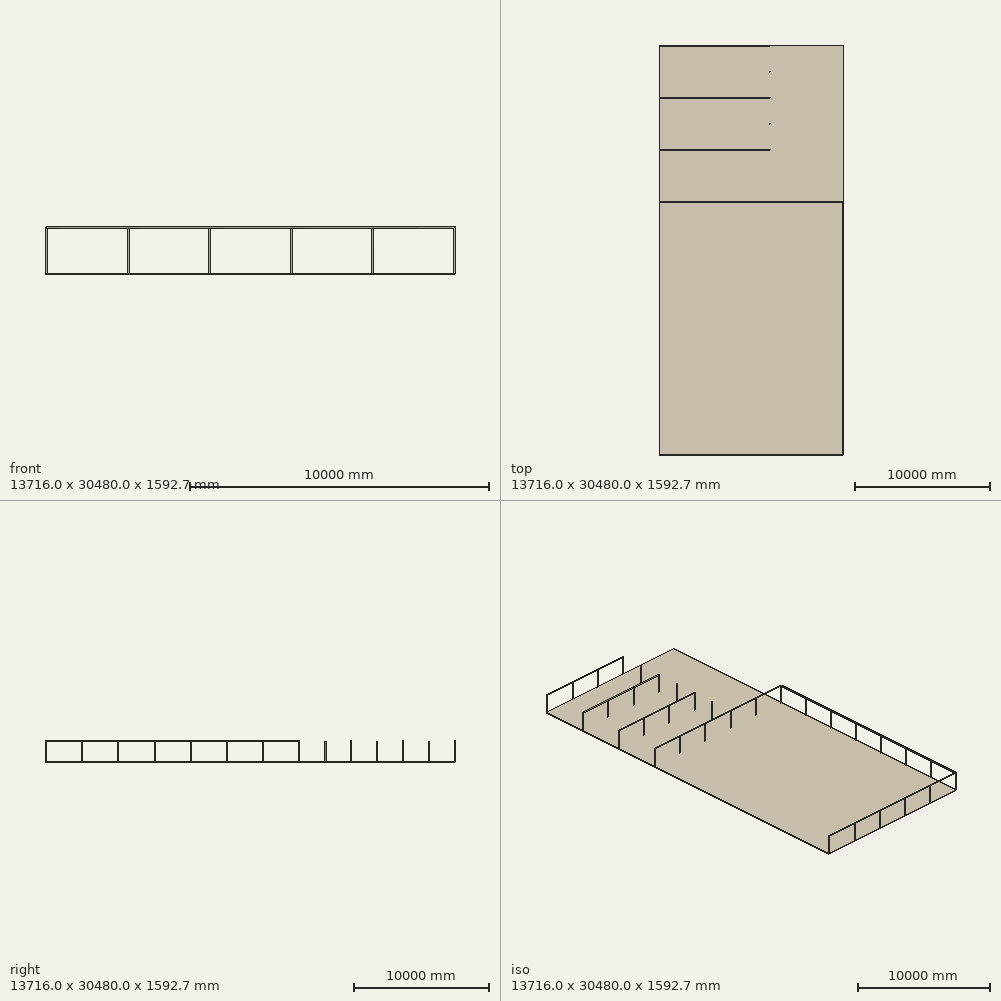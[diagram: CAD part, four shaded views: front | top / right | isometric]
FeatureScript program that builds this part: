
annotation { "Feature Type Name" : "Feature", "Feature Type Description" : "" }
export const myFeature = defineFeature(function(context is Context, id is Id, definition is map)
    precondition{}
    {
        {
            var Q0;
            Q0=qCreatedBy(makeId("Top.planeOp"),FACE);
            var sketch = newSketch(context, id + "F0", { "sketchPlane" : qUnion([Q0])});
            skLineSegment(sketch, "E0.bottom", {"start": v(0, 0) * mm, "end": v(13716, 0) * mm});
            skLineSegment(sketch, "E0.top", {"start": v(0, 30480) * mm, "end": v(13716, 30480) * mm});
            skLineSegment(sketch, "E0.left", {"start": v(0, 0) * mm, "end": v(0, 30480) * mm});
            skLineSegment(sketch, "E0.right", {"start": v(13716, 0) * mm, "end": v(13716, 30480) * mm});
            skSolve(sketch);
        }
        {
            var Q0;
            Q0 = qSketchRegion(id + "F0", true);
            extrude(context, id + "F1", {"entities" : qUnion([Q0]), "oppositeDirection" : true, "depth" : 30.48 * mm, "offsetDistance" : 30.48 * mm});
        }
        {
            var Q0;
            Q0=makeQuery(id+"F1.opExtrude","CAP_FACE",FACE,{"disambiguationData":[OSD([sQuery(id+"F0.wireOp",EDGE,"E0.bottom"),sQuery(id+"F0.wireOp",EDGE,"E0.top"),sQuery(id+"F0.wireOp",EDGE,"E0.left"),sQuery(id+"F0.wireOp",EDGE,"E0.right")])],"isStart":true});
            var sketch = newSketch(context, id + "F2", { "sketchPlane" : qUnion([Q0])});
            skLineSegment(sketch, "E1", {"start": v(38.1, 38.1) * mm, "end": v(2765.45, 38.1) * mm, "construction": true});
            skLineSegment(sketch, "E2", {"start": v(2765.45, 38.1) * mm, "end": v(5492.8, 38.1) * mm, "construction": true});
            skLineSegment(sketch, "E3", {"start": v(5492.8, 38.1) * mm, "end": v(8220.15, 38.1) * mm, "construction": true});
            skLineSegment(sketch, "E4", {"start": v(8220.15, 38.1) * mm, "end": v(10947.5, 38.1) * mm, "construction": true});
            skLineSegment(sketch, "E5", {"start": v(10947.5, 38.1) * mm, "end": v(13674.85, 38.1) * mm, "construction": true});
            skLineSegment(sketch, "E6", {"start": v(13674.85, 38.1) * mm, "end": v(13674.85, 2726.87) * mm, "construction": true});
            skLineSegment(sketch, "E7", {"start": v(13674.85, 2726.87) * mm, "end": v(13674.85, 5415.64) * mm, "construction": true});
            skLineSegment(sketch, "E8", {"start": v(13674.85, 5415.64) * mm, "end": v(13674.85, 8104.41) * mm, "construction": true});
            skLineSegment(sketch, "E9", {"start": v(13674.85, 8104.41) * mm, "end": v(13674.85, 10793.19) * mm, "construction": true});
            skLineSegment(sketch, "E10", {"start": v(13674.85, 10793.19) * mm, "end": v(13674.85, 13481.96) * mm, "construction": true});
            skLineSegment(sketch, "E11", {"start": v(13674.85, 13481.96) * mm, "end": v(13674.85, 16170.73) * mm, "construction": true});
            skLineSegment(sketch, "E12", {"start": v(13674.85, 16170.73) * mm, "end": v(13674.85, 18859.5) * mm, "construction": true});
            skLineSegment(sketch, "E13", {"start": v(13674.85, 18859.5) * mm, "end": v(10947.5, 18859.5) * mm, "construction": true});
            skLineSegment(sketch, "E14", {"start": v(10947.5, 18859.5) * mm, "end": v(8220.15, 18859.5) * mm, "construction": true});
            skLineSegment(sketch, "E15", {"start": v(8220.15, 18859.5) * mm, "end": v(5492.8, 18859.5) * mm, "construction": true});
            skLineSegment(sketch, "E16", {"start": v(5492.8, 18859.5) * mm, "end": v(2765.45, 18859.5) * mm, "construction": true});
            skLineSegment(sketch, "E17", {"start": v(2765.45, 18859.5) * mm, "end": v(38.1, 18859.5) * mm, "construction": true});
            skLineSegment(sketch, "E18", {"start": v(38.1, 18859.5) * mm, "end": v(38.1, 22720.3) * mm, "construction": true});
            skLineSegment(sketch, "E19", {"start": v(38.1, 22720.3) * mm, "end": v(38.1, 26581.1) * mm, "construction": true});
            skLineSegment(sketch, "E20", {"start": v(38.1, 26581.1) * mm, "end": v(38.1, 30441.9) * mm, "construction": true});
            skLineSegment(sketch, "E21", {"start": v(38.1, 30441.9) * mm, "end": v(2765.45, 30441.9) * mm, "construction": true});
            skLineSegment(sketch, "E22", {"start": v(2765.45, 30441.9) * mm, "end": v(5492.8, 30441.9) * mm, "construction": true});
            skLineSegment(sketch, "E23", {"start": v(5492.8, 30441.9) * mm, "end": v(8220.15, 30441.9) * mm, "construction": true});
            skLineSegment(sketch, "E24", {"start": v(38.1, 26581.1) * mm, "end": v(2765.45, 26581.1) * mm, "construction": true});
            skLineSegment(sketch, "E25", {"start": v(2765.45, 26581.1) * mm, "end": v(5492.8, 26581.1) * mm, "construction": true});
            skLineSegment(sketch, "E26", {"start": v(5492.8, 26581.1) * mm, "end": v(8220.15, 26581.1) * mm, "construction": true});
            skLineSegment(sketch, "E27", {"start": v(8220.15, 26581.1) * mm, "end": v(8220.15, 28536.9) * mm, "construction": true});
            skLineSegment(sketch, "E28", {"start": v(38.1, 22720.3) * mm, "end": v(2765.45, 22720.3) * mm, "construction": true});
            skLineSegment(sketch, "E29", {"start": v(2765.45, 22720.3) * mm, "end": v(5492.8, 22720.3) * mm, "construction": true});
            skLineSegment(sketch, "E30", {"start": v(5492.8, 22720.3) * mm, "end": v(8220.15, 22720.3) * mm, "construction": true});
            skLineSegment(sketch, "E31", {"start": v(8220.15, 22720.3) * mm, "end": v(8220.15, 24676.1) * mm, "construction": true});
            skLineSegment(sketch, "E32", {"start": v(8220.15, 18859.5) * mm, "end": v(8220.15, 20815.3) * mm, "construction": true});
            skCircle(sketch, "E33", {"center": v(38.1, 30441.9) * mm, "radius": 38.1 * mm});
            skCircle(sketch, "E34", {"center": v(38.1, 38.1) * mm, "radius": 38.1 * mm});
            skCircle(sketch, "E35", {"center": v(13674.85, 38.1) * mm, "radius": 38.1 * mm});
            skCircle(sketch, "E36", {"center": v(2765.45, 38.1) * mm, "radius": 38.1 * mm});
            skCircle(sketch, "E37", {"center": v(5492.8, 38.1) * mm, "radius": 38.1 * mm});
            skCircle(sketch, "E38", {"center": v(8220.15, 38.1) * mm, "radius": 38.1 * mm});
            skCircle(sketch, "E39", {"center": v(10947.5, 38.1) * mm, "radius": 38.1 * mm});
            skCircle(sketch, "E40", {"center": v(13674.85, 2726.87) * mm, "radius": 38.1 * mm});
            skCircle(sketch, "E41", {"center": v(13674.85, 5415.64) * mm, "radius": 38.1 * mm});
            skCircle(sketch, "E42", {"center": v(13674.85, 8104.41) * mm, "radius": 38.1 * mm});
            skCircle(sketch, "E43", {"center": v(13674.85, 10793.19) * mm, "radius": 38.1 * mm});
            skCircle(sketch, "E44", {"center": v(13674.85, 13481.96) * mm, "radius": 38.1 * mm});
            skCircle(sketch, "E45", {"center": v(13674.85, 16170.73) * mm, "radius": 38.1 * mm});
            skCircle(sketch, "E46", {"center": v(13674.85, 18859.5) * mm, "radius": 38.1 * mm});
            skCircle(sketch, "E47", {"center": v(10947.5, 18859.5) * mm, "radius": 38.1 * mm});
            skCircle(sketch, "E48", {"center": v(8220.15, 18859.5) * mm, "radius": 38.1 * mm});
            skCircle(sketch, "E49", {"center": v(5492.8, 18859.5) * mm, "radius": 38.1 * mm});
            skCircle(sketch, "E50", {"center": v(2765.45, 18859.5) * mm, "radius": 38.1 * mm});
            skCircle(sketch, "E51", {"center": v(38.1, 18859.5) * mm, "radius": 38.1 * mm});
            skCircle(sketch, "E52", {"center": v(8220.15, 20815.3) * mm, "radius": 38.1 * mm});
            skCircle(sketch, "E53", {"center": v(8220.15, 22720.3) * mm, "radius": 38.1 * mm});
            skCircle(sketch, "E54", {"center": v(38.1, 22720.3) * mm, "radius": 38.1 * mm});
            skCircle(sketch, "E55", {"center": v(2765.45, 22720.3) * mm, "radius": 38.1 * mm});
            skCircle(sketch, "E56", {"center": v(5492.8, 22720.3) * mm, "radius": 38.1 * mm});
            skCircle(sketch, "E57", {"center": v(8220.15, 24676.1) * mm, "radius": 38.1 * mm});
            skCircle(sketch, "E58", {"center": v(38.1, 26581.1) * mm, "radius": 38.1 * mm});
            skCircle(sketch, "E59", {"center": v(2765.45, 26581.1) * mm, "radius": 38.1 * mm});
            skCircle(sketch, "E60", {"center": v(5492.8, 26581.1) * mm, "radius": 38.1 * mm});
            skCircle(sketch, "E61", {"center": v(8220.15, 26581.1) * mm, "radius": 38.1 * mm});
            skCircle(sketch, "E62", {"center": v(2765.45, 30441.9) * mm, "radius": 38.1 * mm});
            skCircle(sketch, "E63", {"center": v(5492.8, 30441.9) * mm, "radius": 38.1 * mm});
            skCircle(sketch, "E64", {"center": v(8220.15, 30441.9) * mm, "radius": 38.1 * mm});
            skCircle(sketch, "E65", {"center": v(8220.15, 28536.9) * mm, "radius": 38.1 * mm});
            skSolve(sketch);
        }
        {
            var Q0;
            Q0 = qSketchRegion(id + "F2", true);
            extrude(context, id + "F3", {"entities" : qUnion([Q0]), "operationType" : NewBodyOperationType.ADD, "depth" : 1524 * mm, "offsetDistance" : 30.48 * mm});
        }
        {
            var Q0;
            Q0=makeQuery(id+"F1.opExtrude","SWEPT_FACE",FACE,{"disambiguationData":[OSD([sQuery(id+"F0.wireOp",EDGE,"E0.left")])]});
            cPlane(context, id + "F4", {"entities" : qUnion([Q0]), "cplaneType" : CPlaneType.OFFSET, "offset" : 38.1 * mm, "oppositeDirection" : true, "width" : 152.4 * mm, "height" : 152.4 * mm});
        }
        {
            var Q0;
            Q0=qCreatedBy(id+"F4.planeOp",FACE);
            var sketch = newSketch(context, id + "F5", { "sketchPlane" : qUnion([Q0])});
            skLineSegment(sketch, "E66", {"start": v(-38.1, 1524) * mm, "end": v(-18859.5, 1524) * mm, "construction": true});
            skLineSegment(sketch, "E67", {"start": v(-18859.5, 1524) * mm, "end": v(-22720.3, 1524) * mm, "construction": true});
            skLineSegment(sketch, "E68", {"start": v(-22720.3, 1524) * mm, "end": v(-26581.1, 1524) * mm, "construction": true});
            skLineSegment(sketch, "E69", {"start": v(-26581.1, 1524) * mm, "end": v(-30441.9, 1524) * mm, "construction": true});
            skLineSegment(sketch, "E70", {"start": v(-38.1, 1524) * mm, "end": v(-38.1, 1524) * mm});
            skLineSegment(sketch, "E71", {"start": v(-18859.5, 1524) * mm, "end": v(-18859.5, 1524) * mm});
            skLineSegment(sketch, "E72", {"start": v(-22720.3, 1524) * mm, "end": v(-22720.3, 1524) * mm});
            skLineSegment(sketch, "E73", {"start": v(-26581.1, 1524) * mm, "end": v(-26581.1, 1524) * mm});
            skLineSegment(sketch, "E74", {"start": v(-30441.9, 1524) * mm, "end": v(-30441.9, 1524) * mm});
            skCircle(sketch, "E75", {"center": v(-38.1, 1524) * mm, "radius": 38.1 * mm});
            skCircle(sketch, "E76", {"center": v(-18859.5, 1524) * mm, "radius": 38.1 * mm});
            skCircle(sketch, "E77", {"center": v(-22720.3, 1524) * mm, "radius": 38.1 * mm});
            skCircle(sketch, "E78", {"center": v(-26581.1, 1524) * mm, "radius": 38.1 * mm});
            skCircle(sketch, "E79", {"center": v(-30441.9, 1524) * mm, "radius": 38.1 * mm});
            skSolve(sketch);
        }
        {
            var Q0;
            Q0=makeQuery(id+"F5.imprint","IMPRINT",FACE,{"disambiguationData":[TD([[makeQuery(id+"F5.imprint","IMPRINT",EDGE,{"derivedFrom":sQuery(id+"F5.wireOp",EDGE,"E75")}),1.0]])]});
            var Q1;
            Q1=makeQuery(id+"F5.imprint","IMPRINT",FACE,{"disambiguationData":[TD([[makeQuery(id+"F5.imprint","IMPRINT",EDGE,{"derivedFrom":sQuery(id+"F5.wireOp",EDGE,"E76")}),1.0]])]});
            var Q2;
            Q2=sQuery(id+"F5.wireOp",EDGE,"E75");
            var Q3;
            Q3=sQuery(id+"F5.wireOp",EDGE,"E76");
            extrude(context, id + "F6", {"entities" : qUnion([Q0, Q1]), "operationType" : NewBodyOperationType.ADD, "surfaceEntities" : qUnion([Q2, Q3]), "oppositeDirection" : true, "depth" : 13639.8 * mm, "offsetDistance" : 30.48 * mm});
        }
        {
            var Q0;
            Q0=makeQuery(id+"F5.imprint","IMPRINT",FACE,{"disambiguationData":[TD([[makeQuery(id+"F5.imprint","IMPRINT",EDGE,{"derivedFrom":sQuery(id+"F5.wireOp",EDGE,"E77")}),1.0]])]});
            var Q1;
            Q1=makeQuery(id+"F5.imprint","IMPRINT",FACE,{"disambiguationData":[TD([[makeQuery(id+"F5.imprint","IMPRINT",EDGE,{"derivedFrom":sQuery(id+"F5.wireOp",EDGE,"E78")}),1.0]])]});
            var Q2;
            Q2=makeQuery(id+"F5.imprint","IMPRINT",FACE,{"disambiguationData":[TD([[makeQuery(id+"F5.imprint","IMPRINT",EDGE,{"derivedFrom":sQuery(id+"F5.wireOp",EDGE,"E79")}),1.0]])]});
            extrude(context, id + "F7", {"entities" : qUnion([Q0, Q1, Q2]), "operationType" : NewBodyOperationType.ADD, "oppositeDirection" : true, "depth" : 8153.4 * mm, "offsetDistance" : 30.48 * mm});
        }
        {
            var Q0;
            Q0=sQuery(id+"F2.wireOp",EDGE,"E17");
            cPoint(context, id + "F8", {"entities" : qUnion([Q0]), "parameter" : 0.5});
        }
        {
            var Q0;
            Q0=makeQuery(id+"F1.opExtrude","SWEPT_FACE",FACE,{"disambiguationData":[OSD([sQuery(id+"F0.wireOp",EDGE,"E0.bottom")])]});
            var Q1;
            Q1 = qCreatedBy(id + "F8" ,VERTEX);
            cPlane(context, id + "F9", {"entities" : qUnion([Q0, Q1]), "cplaneType" : CPlaneType.PLANE_POINT, "offset" : 38.1 * mm, "oppositeDirection" : true, "width" : 152.4 * mm, "height" : 152.4 * mm});
        }
        {
            var Q0;
            Q0=qCreatedBy(id+"F9.planeOp",FACE);
            var sketch = newSketch(context, id + "F10", { "sketchPlane" : qUnion([Q0])});
            skCircle(sketch, "E80", {"center": v(13674.85, 1524.12) * mm, "radius": 38.1 * mm});
            skLineSegment(sketch, "E81", {"start": v(13674.85, 1524.12) * mm, "end": v(13674.85, 0) * mm, "construction": true});
            skLineSegment(sketch, "E82", {"start": v(13674.85, 1524.12) * mm, "end": v(8220.15, 1524.12) * mm, "construction": true});
            skCircle(sketch, "E83", {"center": v(8220.15, 1524.12) * mm, "radius": 38.1 * mm});
            skLineSegment(sketch, "E84", {"start": v(8220.15, 1524.12) * mm, "end": v(8220.15, 0) * mm, "construction": true});
            skSolve(sketch);
        }
        {
            var Q0;
            Q0=makeQuery(id+"F10.imprint","IMPRINT",FACE,{"disambiguationData":[TD([[makeQuery(id+"F10.imprint","IMPRINT",EDGE,{"derivedFrom":sQuery(id+"F10.wireOp",EDGE,"E80")}),1.0]])]});
            var Q1;
            Q1=sQuery(id+"F10.wireOp",EDGE,"E80");
            extrude(context, id + "F11", {"entities" : qUnion([Q0]), "operationType" : NewBodyOperationType.ADD, "surfaceEntities" : qUnion([Q1]), "depth" : 18821.4 * mm, "offsetDistance" : 30.48 * mm});
        }
    });
